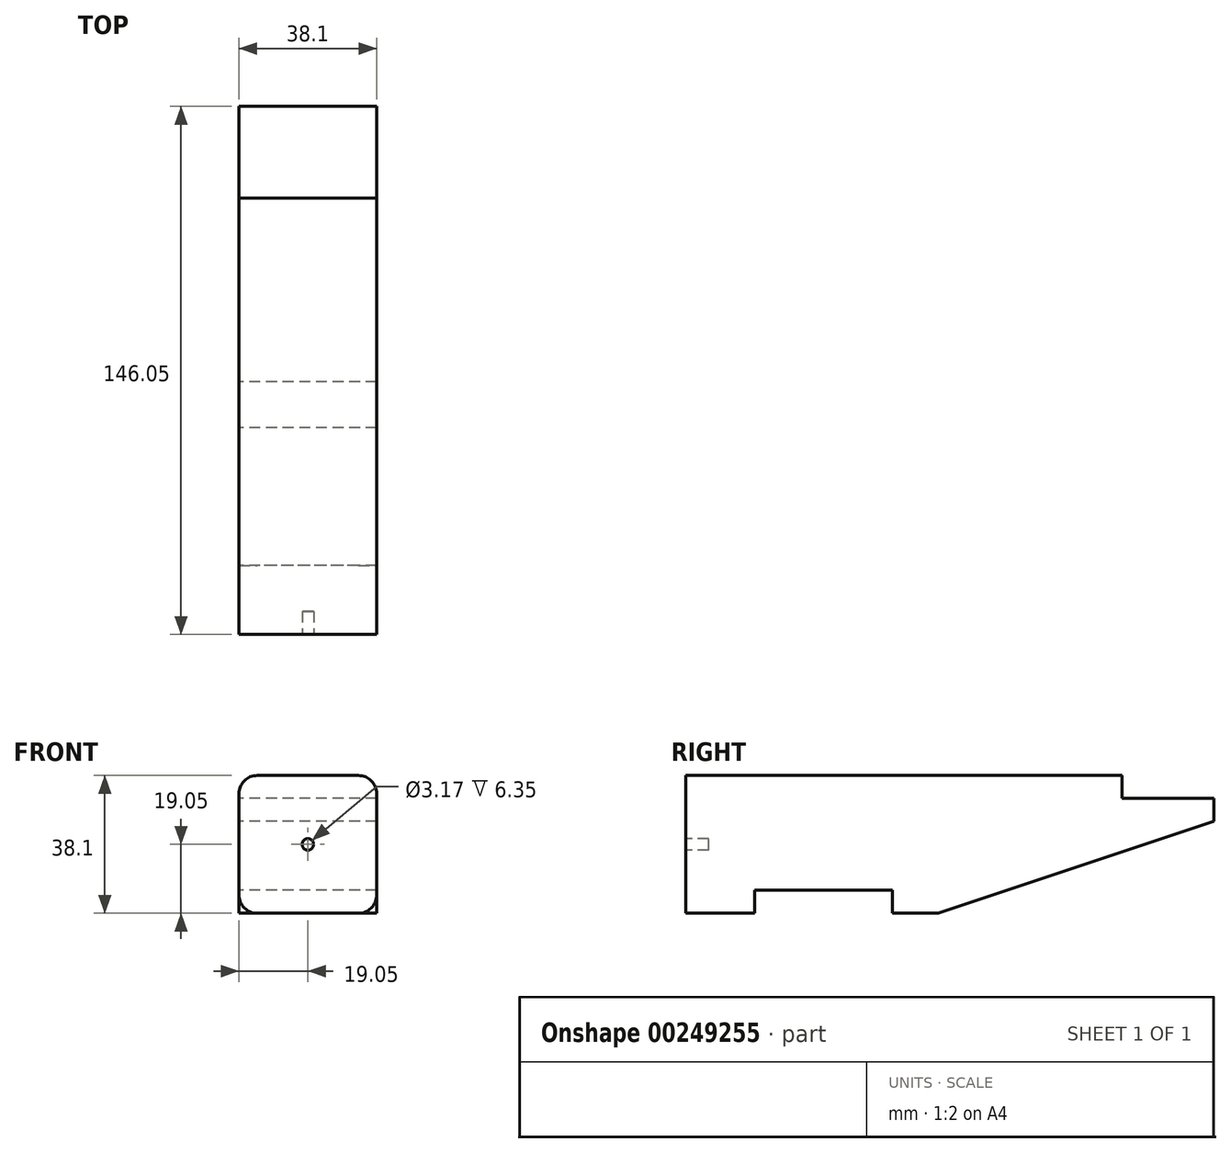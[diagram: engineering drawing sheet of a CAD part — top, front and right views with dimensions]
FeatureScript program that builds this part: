
annotation { "Feature Type Name" : "Feature", "Feature Type Description" : "" }
export const myFeature = defineFeature(function(context is Context, id is Id, definition is map)
    precondition{}
    {
        {
            var Q0;
            Q0=qCreatedBy(makeId("Right.planeOp"),FACE);
            var sketch = newSketch(context, id + "F0", { "sketchPlane" : qUnion([Q0])});
            skLineSegment(sketch, "E0", {"start": v(0, 0) * mm, "end": v(120.65, 0) * mm});
            skLineSegment(sketch, "E1", {"start": v(120.65, 0) * mm, "end": v(120.65, -6.35) * mm});
            skLineSegment(sketch, "E2", {"start": v(120.65, -6.35) * mm, "end": v(146.05, -6.35) * mm});
            skLineSegment(sketch, "E3", {"start": v(0, 0) * mm, "end": v(0, -38.1) * mm});
            skLineSegment(sketch, "E4", {"start": v(0, -38.1) * mm, "end": v(19.05, -38.1) * mm});
            skLineSegment(sketch, "E5", {"start": v(19.05, -38.1) * mm, "end": v(19.05, -31.75) * mm});
            skLineSegment(sketch, "E6", {"start": v(19.05, -31.75) * mm, "end": v(57.15, -31.75) * mm});
            skLineSegment(sketch, "E7", {"start": v(57.15, -31.75) * mm, "end": v(57.15, -38.1) * mm});
            skLineSegment(sketch, "E8", {"start": v(57.15, -38.1) * mm, "end": v(69.85, -38.1) * mm});
            skLineSegment(sketch, "E9", {"start": v(146.05, -6.35) * mm, "end": v(146.05, -12.7) * mm});
            skLineSegment(sketch, "E10", {"start": v(146.05, -12.7) * mm, "end": v(69.85, -38.1) * mm});
            skSolve(sketch);
        }
        {
            var Q0;
            Q0=makeQuery(id+"F0.imprint","IMPRINT",FACE,{"disambiguationData":[TD([[makeQuery(id+"F0.imprint","IMPRINT",EDGE,{"derivedFrom":sQuery(id+"F0.wireOp",EDGE,"E0")}),-1.0]])]});
            extrude(context, id + "F1", {"entities" : qUnion([Q0]), "depth" : 38.1 * mm});
        }
        {
            var Q0;
            Q0=makeQuery(id+"F1.opExtrude","SWEPT_FACE",FACE,{"disambiguationData":[OSD([sQuery(id+"F0.wireOp",EDGE,"E3")])]});
            var sketch = newSketch(context, id + "F2", { "sketchPlane" : qUnion([Q0])});
            skPoint(sketch, "E11", {"position": v(19.05, -19.05) * mm});
            skCircle(sketch, "E12", {"center": v(19.05, -19.05) * mm, "radius": 1.59 * mm});
            skSolve(sketch);
        }
        {
            var Q0;
            Q0=makeQuery(id+"F2.imprint","IMPRINT",FACE,{"disambiguationData":[TD([[makeQuery(id+"F2.imprint","IMPRINT",EDGE,{"derivedFrom":sQuery(id+"F2.wireOp",EDGE,"E12")}),1.0]])]});
            extrude(context, id + "F3", {"entities" : qUnion([Q0]), "operationType" : NewBodyOperationType.REMOVE, "oppositeDirection" : true, "depth" : 6.35 * mm});
        }
        {
            var Q0;
            Q0=makeQuery(id+"F1.opExtrude","CAP_EDGE",EDGE,{"disambiguationData":[OSD([sQuery(id+"F0.wireOp",EDGE,"E0")])],"isStart":false});
            var Q1;
            Q1=makeQuery(id+"F1.opExtrude","CAP_EDGE",EDGE,{"disambiguationData":[OSD([sQuery(id+"F0.wireOp",EDGE,"E0")])],"isStart":true});
            var Q2;
            Q2=makeQuery(id+"F1.opExtrude","CAP_EDGE",EDGE,{"disambiguationData":[OSD([sQuery(id+"F0.wireOp",EDGE,"E4")])],"isStart":false});
            var Q3;
            Q3=makeQuery(id+"F1.opExtrude","CAP_EDGE",EDGE,{"disambiguationData":[OSD([sQuery(id+"F0.wireOp",EDGE,"E4")])],"isStart":true});
            fillet(context, id + "F4", {"entities" : qUnion([Q0, Q1, Q2, Q3]), "radius" : 5.08 * mm, "tangentPropagation" : true, "allowEdgeOverflow" : false});
        }
    });
